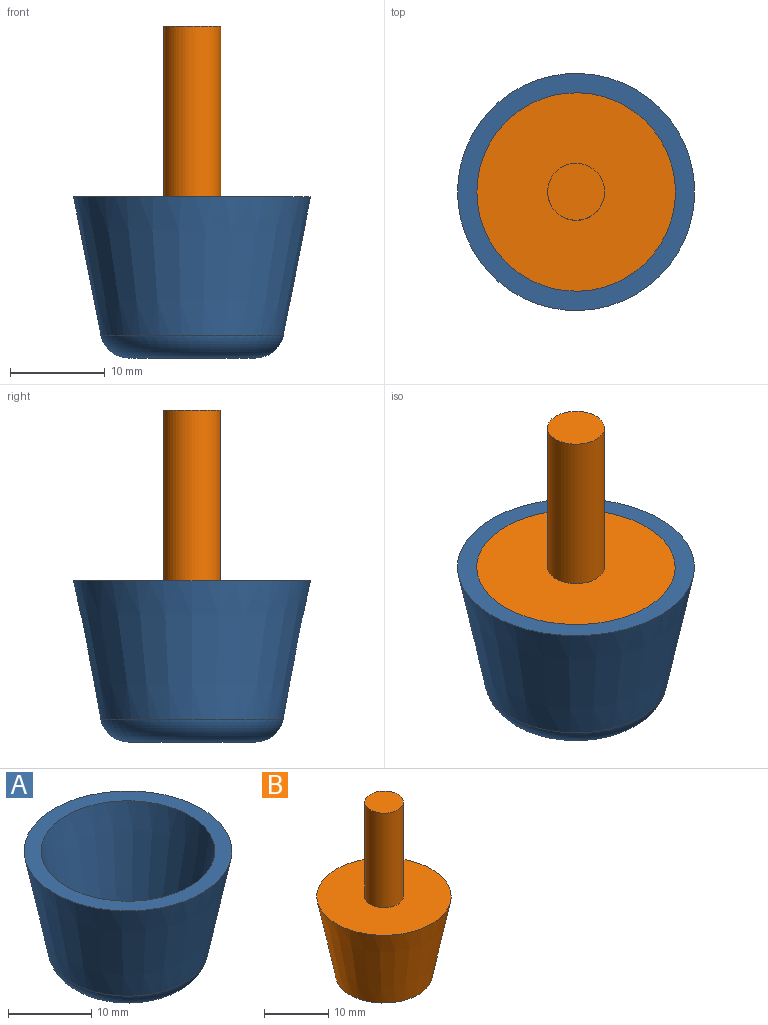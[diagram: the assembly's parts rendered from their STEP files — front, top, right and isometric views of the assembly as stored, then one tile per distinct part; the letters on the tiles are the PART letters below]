
ASSEMBLY  parts=2 mates=1
PART A: 6 faces, bbox 25x25x17 mm
  f0: plane 25x25mm, normal (0,0,1), area 147.1mm2, adj f1,f4
  f1: cone r=10.46mm half-angle=11.2deg, axis (0,0,1), area 862.7mm2, adj f0,f2
  f2: plane 15x15mm, normal (0,0,1), area 176.7mm2, adj f1
  f3: plane 13.36x13.36mm, normal (0,0,-1), area 140.1mm2, adj f5
  f4: cone r=12.5mm half-angle=11.2deg, axis (0,0,1), area 1032.9mm2, adj f0,f5
  f5: torus R=6.68mm, axis (0,0,1), area 218.8mm2, adj f3,f4
PART B: 5 faces, bbox 20.9x20.9x33 mm
  f0: plane 15x15mm, normal (0,0,-1), area 176.7mm2, adj f1
  f1: cone r=10.46mm half-angle=11.2deg, axis (0,0,1), area 862.7mm2, adj f0,f2
  f2: plane 20.92x20.92mm, normal (0,0,1), area 315.5mm2, adj f1,f3
  f3: cylinder r=3mm len=18mm, axis (0,0,-1), area 339.3mm2, adj f2,f4
  f4: plane 6x6mm, normal (0,0,1), area 28.3mm2, adj f3
PLACE A at identity fixed
PLACE B at identity
MATE fastened A.f1 <-> B.f1  axis (0,0,1) through (0,0,2)mm
